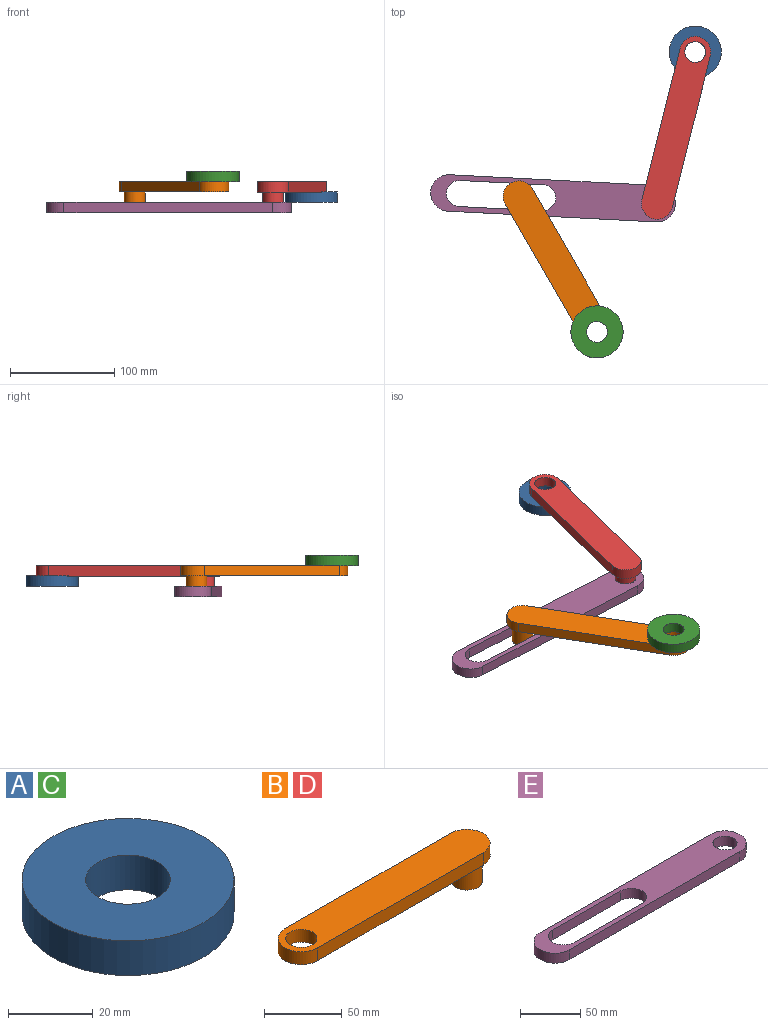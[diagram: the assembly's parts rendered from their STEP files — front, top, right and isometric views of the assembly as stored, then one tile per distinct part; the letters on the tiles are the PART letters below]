
ASSEMBLY  parts=5 mates=4
PART A: 4 faces, bbox 50x50x10 mm
  f0: cylinder r=10mm len=20mm, axis (0,0,-1), area 628.3mm2, adj f2,f3
  f1: cylinder r=25mm len=50mm, axis (0,0,-1), area 1570.8mm2, adj f2,f3
  f2: plane 50x50mm, normal (0,0,1), area 1649.3mm2, adj f0,f1
  f3: plane 50x50mm, normal (0,0,-1), area 1649.3mm2, adj f0,f1
PART B: 9 faces, bbox 180x30x30 mm
  f0: plane 150x10mm, normal (0,-1,0), area 1500mm2, adj f1,f4,f5,f6
  f1: cylinder r=15mm len=30mm, axis (0,0,-1), area 471.2mm2, adj f0,f2,f5,f6
  f2: plane 150x10mm, normal (0,1,0), area 1500mm2, adj f1,f4,f5,f6
  f3: cylinder r=10mm len=20mm, axis (0,0,-1), area 628.3mm2, adj f5,f6
  f4: cylinder r=15mm len=30mm, axis (0,0,-1), area 471.2mm2, adj f0,f2,f5,f6
  f5: plane 180x30mm, normal (0,0,1), area 4892.7mm2, adj f0,f1,f2,f3,f4
  f6: plane 180x30mm, normal (0,0,-1), area 4578.5mm2, adj f0,f1,f2,f3,f4,f7
  f7: cylinder r=10mm len=20mm, axis (0,0,1), area 1256.6mm2, adj f6,f8
  f8: plane 20x20mm, normal (0,0,-1), area 314.2mm2, adj f7
PART C: same geometry as A
PART D: same geometry as B
PART E: 11 faces, bbox 235x35x10 mm
  f0: cylinder r=17.5mm len=35mm, axis (0,0,-1), area 549.8mm2, adj f1,f8,f9,f10
  f1: plane 200x10mm, normal (0,-1,0), area 2000mm2, adj f0,f2,f9,f10
  f2: cylinder r=17.5mm len=35mm, axis (0,0,-1), area 549.8mm2, adj f1,f8,f9,f10
  f3: plane 80x10mm, normal (0,1,0), area 800mm2, adj f4,f6,f9,f10
  f4: cylinder r=12.5mm len=25mm, axis (0,0,-1), area 392.7mm2, adj f3,f5,f9,f10
  f5: plane 80x10mm, normal (0,-1,0), area 800mm2, adj f4,f6,f9,f10
  f6: cylinder r=12.5mm len=25mm, axis (0,0,-1), area 392.7mm2, adj f3,f5,f9,f10
  f7: cylinder r=10mm len=20mm, axis (0,0,-1), area 628.3mm2, adj f9,f10
  f8: plane 200x10mm, normal (0,1,0), area 2000mm2, adj f0,f2,f9,f10
  f9: plane 235x35mm, normal (0,0,1), area 5157.1mm2, adj f0,f1,f2,f3,f4,f5,f6,f7
  f10: plane 235x35mm, normal (0,0,-1), area 5157.1mm2, adj f0,f1,f2,f3,f4,f5,f6,f7
PLACE A rot(axis=(0,0,1),0.2deg) t=(71.11,270.14,2.44)mm fixed
PLACE B rot(axis=(0,0,1),120deg) t=(-60.61,66.57,12.44)mm
PLACE C t=(-23.11,1.62,22.44)mm fixed
PLACE D rot(axis=(0,0,-1),104.1deg) t=(52.84,197.4,12.44)mm
PLACE E rot(axis=(0,0,-1),3deg) t=(-65.3,129.82,-7.56)mm
MATE revolute C.f0 <-> B.f3  axis (0,0,-1) through (-23.11,1.62,17.44)mm
MATE revolute D.f3 <-> A.f0  axis (0,0,-1) through (71.11,270.14,7.44)mm
MATE revolute D.f1 <-> E.f2  axis (0,0,-1) through (34.57,124.66,-12.56)mm
MATE pin_slot B.f1 <-> E.f4  axis (0,0,-1) through (-98.11,131.52,-12.56)mm
